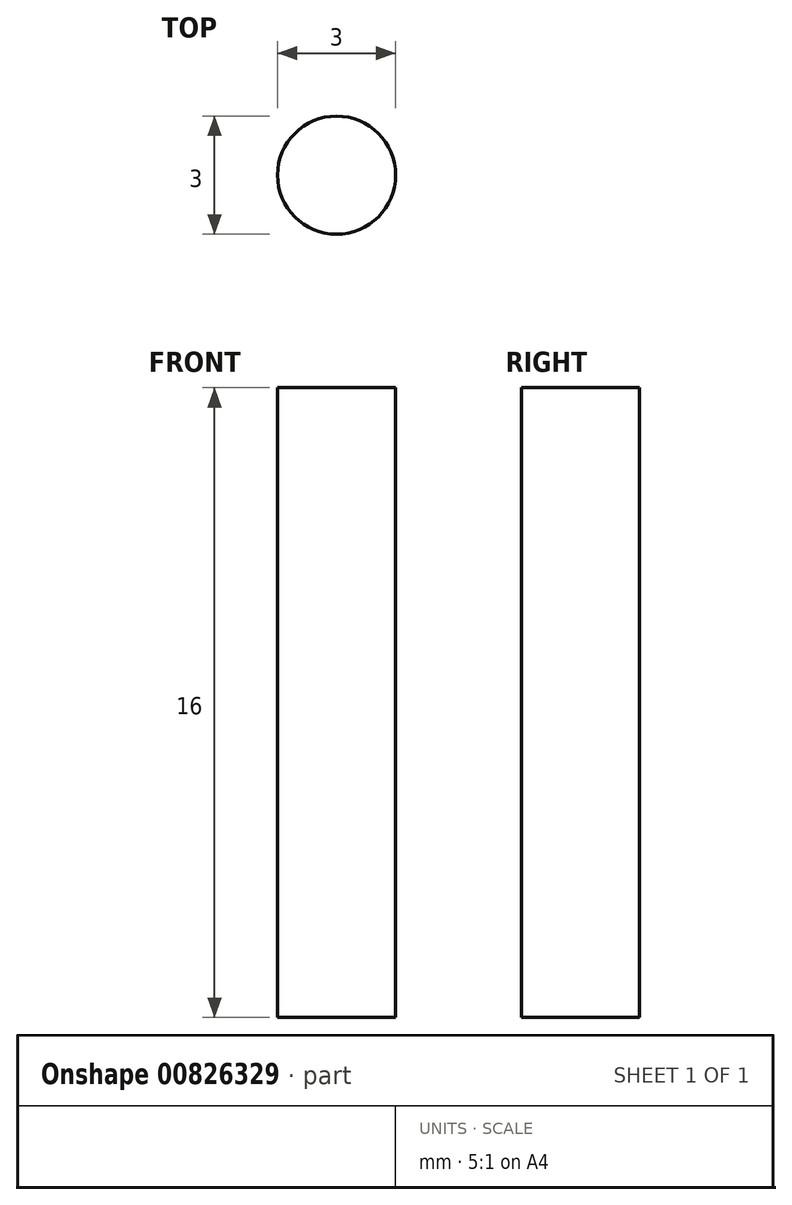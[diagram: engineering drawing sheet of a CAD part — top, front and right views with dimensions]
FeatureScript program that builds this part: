
annotation { "Feature Type Name" : "Feature", "Feature Type Description" : "" }
export const myFeature = defineFeature(function(context is Context, id is Id, definition is map)
    precondition{}
    {
        {
            var Q0;
            Q0=qCreatedBy(makeId("Top.planeOp"),FACE);
            var sketch = newSketch(context, id + "F0", { "sketchPlane" : qUnion([Q0])});
            skCircle(sketch, "E0", {"center": v(0, 0) * mm, "radius": 1.5 * mm});
            skSolve(sketch);
        }
        {
            var Q0;
            Q0=makeQuery(id+"F0.imprint","IMPRINT",FACE,{"disambiguationData":[TD([[makeQuery(id+"F0.imprint","IMPRINT",EDGE,{"derivedFrom":sQuery(id+"F0.wireOp",EDGE,"E0")}),1.0]])]});
            extrude(context, id + "F1", {"entities" : qUnion([Q0]), "depth" : 16 * mm, "offsetDistance" : 25 * mm});
        }
    });
